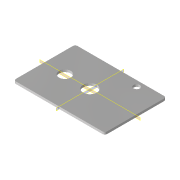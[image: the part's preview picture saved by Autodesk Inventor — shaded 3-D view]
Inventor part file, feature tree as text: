
AUTODESK INVENTOR PART (.ipt)
format: ipt  version: 2022 (Build 260153000, 153)  size: 130,048 bytes
history: native  units: mm
features: other x3, plane x2, extrude x2, sketch x2, projected_geometry x1, reference x1
ambient origin geometry x8: Origin, YZ Plane, XZ Plane, XY Plane, X Axis, Y Axis, Z Axis, Center Point
bodies: Volumenkörper1 (feature_tree), Body1 (feature_tree)
feature tree (11):
  plane  "Work Plane1"
  plane  "Work Plane2"
  extrude  "Extrusion1"  Depth=10.5mm
  extrude  "Extrusion2"  Depth=10.0mm TaperAngle=0.0deg
  sketch  "Sketch1"  dims[d0=9.0mm d1=10.5mm]
  projected_geometry  "Projected Loop1"
  sketch  "Skizze2"  dims[d2=2.5mm d3=10.0mm d4=0.0mm d5=10.0mm d6=0.0mm]
  reference  "Referenz1"
  other  "<userpath>\Documents\GitHub\Matchboxscope\INVENTOR\Anglerfish_bonne_mamman_v0.iam"
  other  "Anglerfish_bonne_mamman_v0.iam"
  other  "Anglerfish_Lightplate_Tislinkbridge:1"
